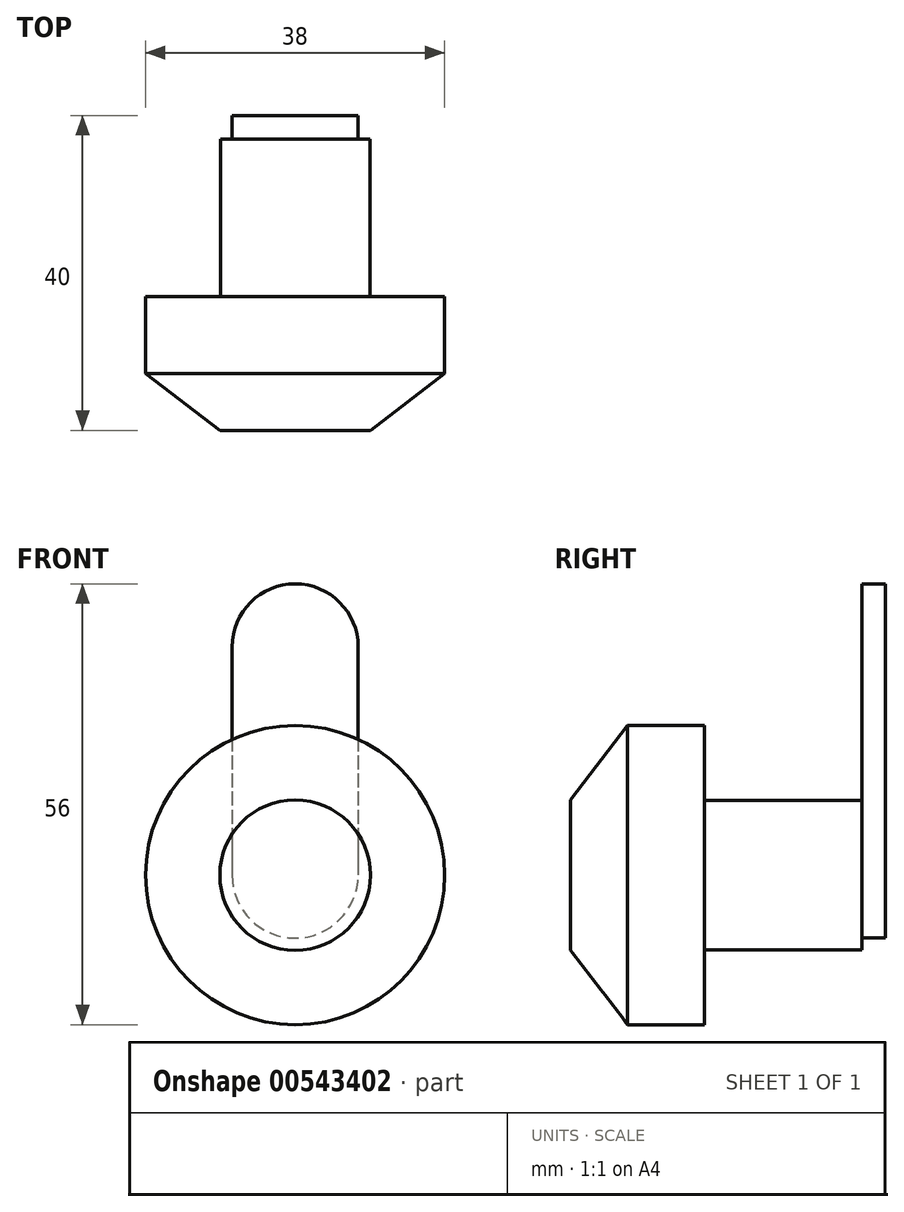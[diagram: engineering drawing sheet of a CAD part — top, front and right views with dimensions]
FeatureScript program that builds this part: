
annotation { "Feature Type Name" : "Feature", "Feature Type Description" : "" }
export const myFeature = defineFeature(function(context is Context, id is Id, definition is map)
    precondition{}
    {
        {
            var Q0;
            Q0=qCreatedBy(makeId("Right.planeOp"),FACE);
            var sketch = newSketch(context, id + "F0", { "sketchPlane" : qUnion([Q0])});
            skLineSegment(sketch, "E0", {"start": v(-43.86, 0) * mm, "end": v(38.06, 0) * mm, "construction": true});
            skLineSegment(sketch, "E1", {"start": v(-18.5, 0) * mm, "end": v(-18.5, 9.56) * mm});
            skLineSegment(sketch, "E2", {"start": v(-18.5, 9.56) * mm, "end": v(-11.26, 19) * mm});
            skLineSegment(sketch, "E3", {"start": v(-11.26, 19) * mm, "end": v(-1.5, 19) * mm});
            skLineSegment(sketch, "E4", {"start": v(-1.5, 19) * mm, "end": v(-1.5, 9.5) * mm});
            skLineSegment(sketch, "E5", {"start": v(-1.5, 9.5) * mm, "end": v(18.5, 9.5) * mm});
            skLineSegment(sketch, "E6", {"start": v(18.5, 9.5) * mm, "end": v(18.5, 0) * mm});
            skLineSegment(sketch, "E7", {"start": v(18.5, 0) * mm, "end": v(-18.5, 0) * mm});
            skSolve(sketch);
        }
        {
            var Q0;
            Q0 = qSketchRegion(id + "F0", true);
            var Q1;
            Q1=sQuery(id+"F0.wireOp",EDGE,"E0");
            revolve(context, id + "F1", {"entities" : qUnion([Q0]), "axis" : qUnion([Q1]), "revolveType" : RevolveType.FULL});
        }
        {
            var Q0;
            Q0=makeQuery(id+"F1.opRevolve","SWEPT_FACE",FACE,{"disambiguationData":[OSD([sQuery(id+"F0.wireOp",EDGE,"E6")])]});
            var sketch = newSketch(context, id + "F2", { "sketchPlane" : qUnion([Q0])});
            skLineSegment(sketch, "E8.left", {"start": v(-8, 29) * mm, "end": v(-8, 0) * mm});
            skLineSegment(sketch, "E8.right", {"start": v(8, 29) * mm, "end": v(8, 0) * mm});
            skArc(sketch, "E9", {"start": v(-8, 0) * mm, "mid": v(0, -8) * mm, "end": v(8, 0) * mm});
            skArc(sketch, "E10", {"start": v(8, 29) * mm, "mid": v(0, 37) * mm, "end": v(-8, 29) * mm});
            skSolve(sketch);
        }
        {
            var Q0;
            {var subQ0=sQuery(id+"F2.wireOp",EDGE,"E10");Q0=makeQuery(id+"F2.imprint","IMPRINT",FACE,{"disambiguationData":[TD([[makeQuery(id+"F2.imprint","IMPRINT",EDGE,{"derivedFrom":subQ0}),1.0]])]});}
            var Q1;
            {var subQ0=sQuery(id+"F2.wireOp",EDGE,"E9");Q1=makeQuery(id+"F2.imprint","IMPRINT",FACE,{"disambiguationData":[TD([[makeQuery(id+"F2.imprint","IMPRINT",EDGE,{"derivedFrom":subQ0}),1.0]])]});}
            extrude(context, id + "F3", {"entities" : qUnion([Q0, Q1]), "operationType" : NewBodyOperationType.ADD, "depth" : 3 * mm, "offsetDistance" : 25.4 * mm});
        }
    });
